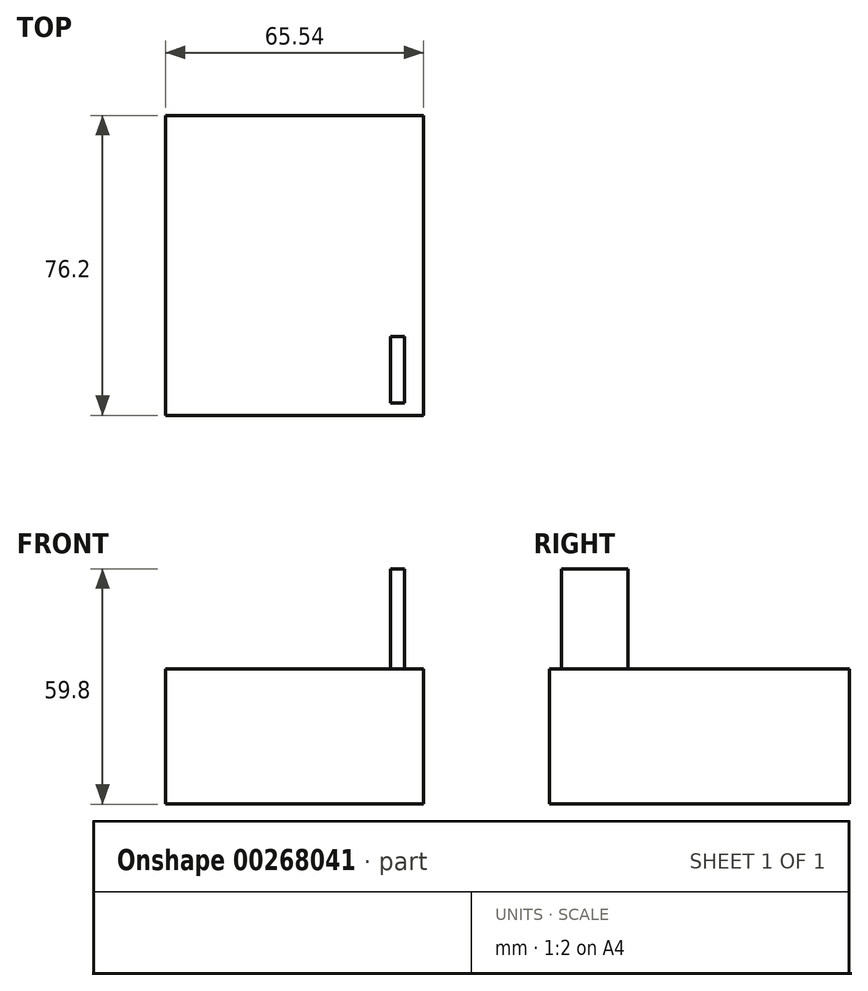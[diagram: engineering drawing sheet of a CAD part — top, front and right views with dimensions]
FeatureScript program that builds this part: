
annotation { "Feature Type Name" : "Feature", "Feature Type Description" : "" }
export const myFeature = defineFeature(function(context is Context, id is Id, definition is map)
    precondition{}
    {
        {
            var Q0;
            Q0=qCreatedBy(makeId("Front.planeOp"),FACE);
            var sketch = newSketch(context, id + "F0", { "sketchPlane" : qUnion([Q0])});
            skLineSegment(sketch, "E0.bottom", {"start": v(32.77, 17.2) * mm, "end": v(-32.77, 17.2) * mm});
            skLineSegment(sketch, "E0.top", {"start": v(32.77, -17.2) * mm, "end": v(-32.77, -17.2) * mm});
            skLineSegment(sketch, "E0.left", {"start": v(32.77, 17.2) * mm, "end": v(32.77, -17.2) * mm});
            skLineSegment(sketch, "E0.right", {"start": v(-32.77, 17.2) * mm, "end": v(-32.77, -17.2) * mm});
            skPoint(sketch, "E0.middle", {"position": v(0, 0) * mm});
            skSolve(sketch);
        }
        {
            var Q0;
            Q0 = qSketchRegion(id + "F0", true);
            extrude(context, id + "F1", {"entities" : qUnion([Q0]), "depth" : 76.2 * mm});
        }
        {
            var Q0;
            Q0=makeQuery(id+"F1.opExtrude","SWEPT_FACE",FACE,{"disambiguationData":[OSD([sQuery(id+"F0.wireOp",EDGE,"E0.bottom")])]});
            var sketch = newSketch(context, id + "F2", { "sketchPlane" : qUnion([Q0])});
            skLineSegment(sketch, "E1.bottom", {"start": v(27.98, -56.25) * mm, "end": v(24.41, -56.25) * mm});
            skLineSegment(sketch, "E1.top", {"start": v(27.98, -73.13) * mm, "end": v(24.41, -73.13) * mm});
            skLineSegment(sketch, "E1.left", {"start": v(27.98, -56.25) * mm, "end": v(27.98, -73.13) * mm});
            skLineSegment(sketch, "E1.right", {"start": v(24.41, -56.25) * mm, "end": v(24.41, -73.13) * mm});
            skSolve(sketch);
        }
        {
            var Q0;
            Q0 = qSketchRegion(id + "F2", true);
            extrude(context, id + "F3", {"entities" : qUnion([Q0]), "operationType" : NewBodyOperationType.ADD, "depth" : 25.4 * mm});
        }
    });
